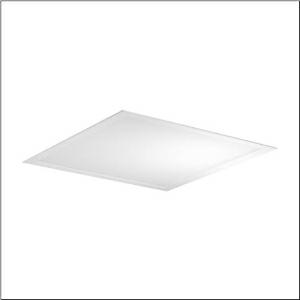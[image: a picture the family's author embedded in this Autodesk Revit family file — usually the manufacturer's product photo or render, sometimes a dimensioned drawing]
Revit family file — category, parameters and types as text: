
# Revit family: apollon_31_square_51mp11w72442
name_source: partatom
category: Lighting Fixtures
units: mm (PartAtom-declared; Revit-internal decimal feet)

## family parameters
Cut with Voids When Loaded = No
Host = Face
Light Source = No
Part Type = Normal
Room Calculation Point = No
Round Connector Dimension = Use Diameter
Shared = No

## types (1)
- Apollon 31 square (1 x LED, 4000 lm, 27.5 W, 4000K)
    Apparent Load = 28 VA
    CIE Flux Codes = 61 87 97 100 100
    Color Rendering = 80
    Color Temperature = 4000K
    Default Elevation = 1800 mm
    Description = Apollon 31 square, office luminaire, primary optical cover: micro prismatic cover, of PMMA, CAT 2 (L<= 3000cd/m²), light emission: direct distribution, primary light characteristic: symmetric, installation type: lay-in mounting, recessed, LED, rated luminous flux: 4.000lm, luminous efficacy: 145lm/W, light colour: 840, colour temperature: 4000K, control gear: ON/OFF, with terminal, 3-pole, mains connection: 220..240V, AC, 50/60Hz, rated input power: 28W, suitable for self-contained emergency lighting element 58DB00B013A with integrated self-test function according to EN 60598-2-22, housing, of aluminium, coated, traffic white (RAL 9016), module: M625, length: 620mm, width: 620mm, height: 62mm, housing upper side, of sheet steel, coated, protection rating (complete): IP20, protection rating (lamp compartment, on room side): IP40, insulation class (complete): insulation class II (safety insulation), certification: CE, ENEC, impact resistance: IK03, permissible operating ambient temperature: -20..+40°C, corresponds to IFS (International Featured Standards) requirements for safety and quality in the food industry, packaging unit: 1 piece
    Height = 0 mm  [stored 0 ft]
    Lamp = 1 x LED
    Lamp Light Flux = 4000 lm
    Lamp Power = 27.5 W
    Lamp count = 1
    Length = 620 mm
    Luminous efficacy = 145 lm/W
    Manufacturer = Siteco
    ModVariant = No
    Model = 51MP11W72442
    Mounting Place = Ceiling
    Mounting Type = Recessed
    Number of Poles = 1
    OnlyDefault = Yes
    Power Factor = 1
    Product Name = Apollon 31 square
    Product group = office luminaire | ceiling recessed
    ProductGroupID = 400
    Protection Class = Protection class II
    Protection Degree = IP 20
    RLX_Detail_Level = 1
    RLX_Emergency_Light_Flux = 0 lm
    RLX_Emergency_Type = 0
    RLX_Emergency_Type_DB = No
    RlxData = <blob elided: 13273 chars, md5=d2b98748>
    Socket = socket
    Standby Power = 0 W
    System Light Flux = 4000 lm
    System Power = 28 W
    Type Comments = Product without accessories
    Type Image = l_1291039.jpg
    URL = http://relux.com
    VarID = ---
    Voltage = 0 V
    Weight = 0.00 kg
    Width = 620 mm

note: [stored X ft] marks values corroborated as IEEE doubles in the binary element streams (Revit-internal decimal feet)

## geometry (parser evidence)
native form markers: Sweep x10
no freeform markers — native parametric forms only
